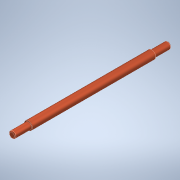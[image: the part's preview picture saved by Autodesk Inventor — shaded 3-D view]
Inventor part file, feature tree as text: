
AUTODESK INVENTOR PART (.ipt)
format: ipt  version: 2021 (Build 250183000, 183)  size: 109,056 bytes
history: native  units: mm
features: extrude x2, sketch x2, other x1, fillet x1, mirror x1
ambient origin geometry x8: Origin, YZ Plane, XZ Plane, XY Plane, X Axis, Y Axis, Z Axis, Center Point
bodies: Body1 (feature_tree)
feature tree (7):
  other  "Sólido1"
  extrude  "Extrusão1"  Depth=300.0mm TaperAngle=0.0deg
  extrude  "Extrusão2"  Depth=40.0mm TaperAngle=0.0deg
  fillet  "Arredondamento1"  Radius=2.0mm
  mirror  "Espelhamento1"
  sketch  "Esboço1"  dims[d0=20.0mm d1=300.0mm d2=0.0mm]
  sketch  "Esboço2"  dims[d3=16.0mm d4=40.0mm d5=0.0mm d6=2.0mm]
